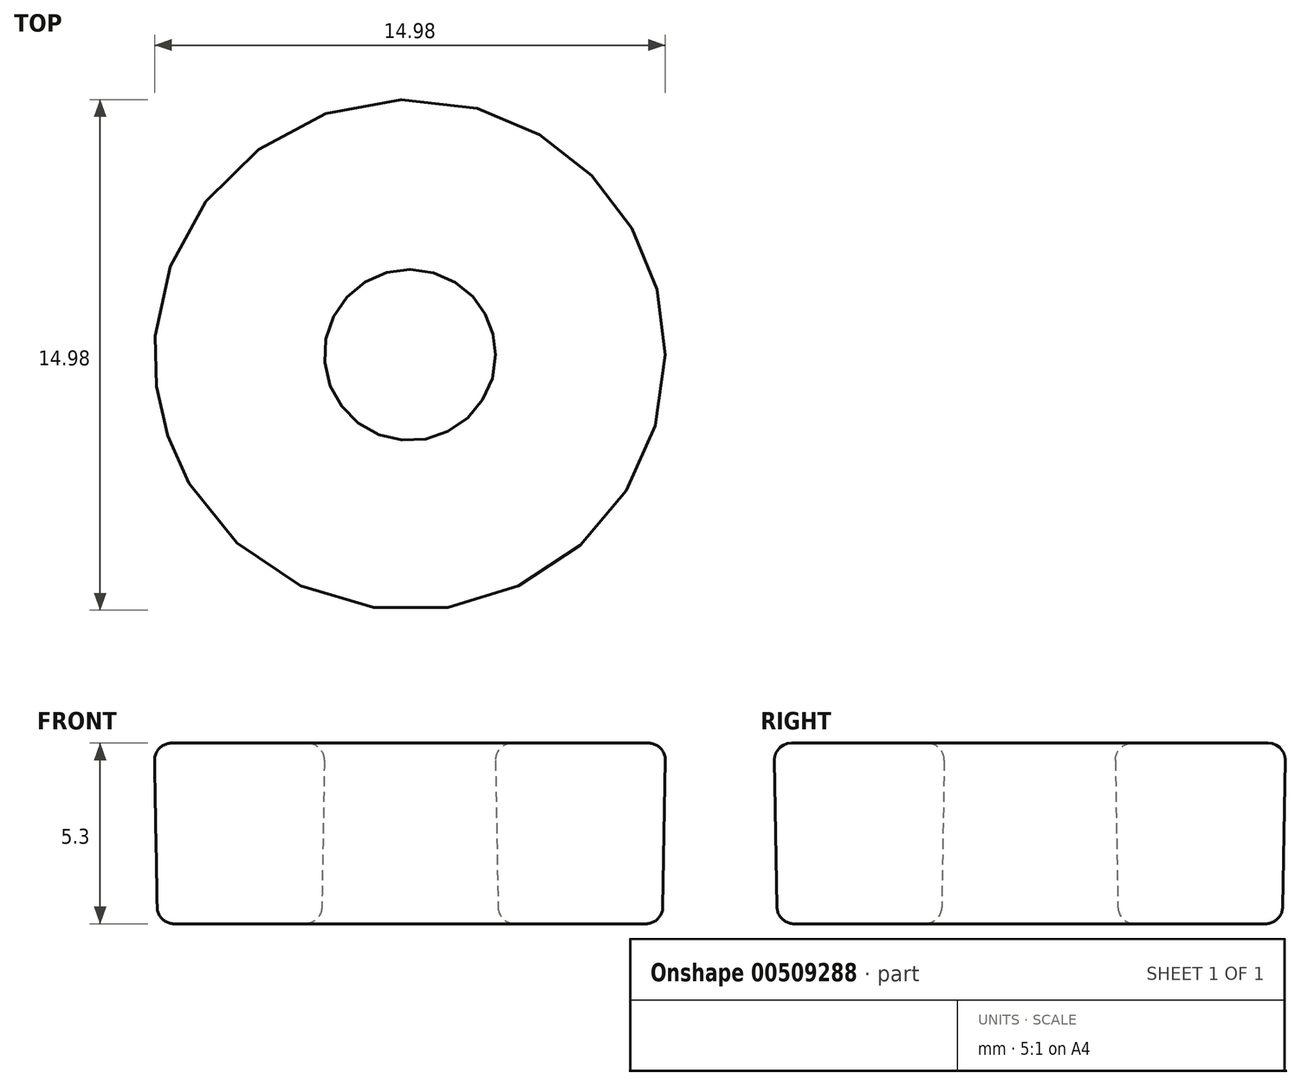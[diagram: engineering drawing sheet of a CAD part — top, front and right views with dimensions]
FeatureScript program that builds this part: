
annotation { "Feature Type Name" : "Feature", "Feature Type Description" : "" }
export const myFeature = defineFeature(function(context is Context, id is Id, definition is map)
    precondition{}
    {
        {
            var Q0;
            Q0=qCreatedBy(makeId("Top.planeOp"),FACE);
            var sketch = newSketch(context, id + "F0", { "sketchPlane" : qUnion([Q0])});
            skCircle(sketch, "E0", {"center": v(0, 0) * mm, "radius": 2.5 * mm});
            skCircle(sketch, "E1", {"center": v(0, 0) * mm, "radius": 7.5 * mm});
            skSolve(sketch);
        }
        {
            var Q0;
            Q0 = qSketchRegion(id + "F0", true);
            extrude(context, id + "F1", {"entities" : qUnion([Q0]), "oppositeDirection" : true, "offsetDistance" : 25 * mm, "depth" : 5.3 * mm, "hasDraft" : true, "draftAngle" : 1 * degree, "draftPullDirection" : true});
        }
        {
            var Q0;
            Q0=makeQuery(id+"F1.opExtrude","CAP_FACE",FACE,{"disambiguationData":[OSD([sQuery(id+"F0.wireOp",EDGE,"E0"),sQuery(id+"F0.wireOp",EDGE,"E1")])],"isStart":false});
            var Q1;
            Q1=makeQuery(id+"F1.opExtrude","CAP_FACE",FACE,{"disambiguationData":[OSD([sQuery(id+"F0.wireOp",EDGE,"E0"),sQuery(id+"F0.wireOp",EDGE,"E1")])],"isStart":true});
            fillet(context, id + "F2", {"entities" : qUnion([Q0, Q1]), "radius" : .5 * mm, "tangentPropagation" : true, "allowEdgeOverflow" : false});
        }
    });
